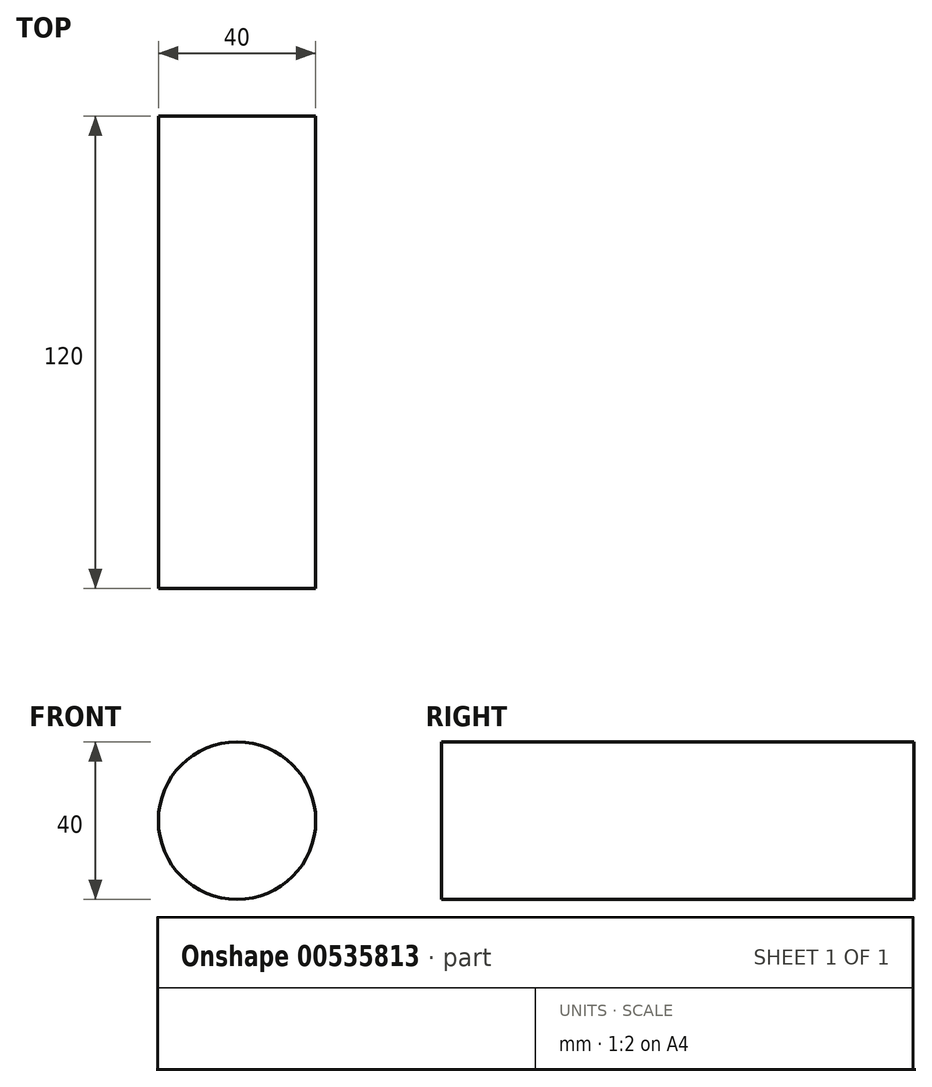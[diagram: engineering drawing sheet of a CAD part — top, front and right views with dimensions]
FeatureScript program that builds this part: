
annotation { "Feature Type Name" : "Feature", "Feature Type Description" : "" }
export const myFeature = defineFeature(function(context is Context, id is Id, definition is map)
    precondition{}
    {
        {
            var Q0;
            Q0=qCreatedBy(makeId("Front.planeOp"),FACE);
            var sketch = newSketch(context, id + "F0", { "sketchPlane" : qUnion([Q0])});
            skCircle(sketch, "E0", {"center": v(0, 0) * mm, "radius": 20 * mm});
            skSolve(sketch);
        }
        {
            var Q0;
            Q0=makeQuery(id+"F0.imprint","IMPRINT",FACE,{"disambiguationData":[TD([[makeQuery(id+"F0.imprint","IMPRINT",EDGE,{"derivedFrom":sQuery(id+"F0.wireOp",EDGE,"E0")}),1.0]])]});
            extrude(context, id + "F1", {"entities" : qUnion([Q0]), "endBound" : BoundingType.SYMMETRIC, "depth" : 120 * mm, "offsetDistance" : 25 * mm});
        }
    });
